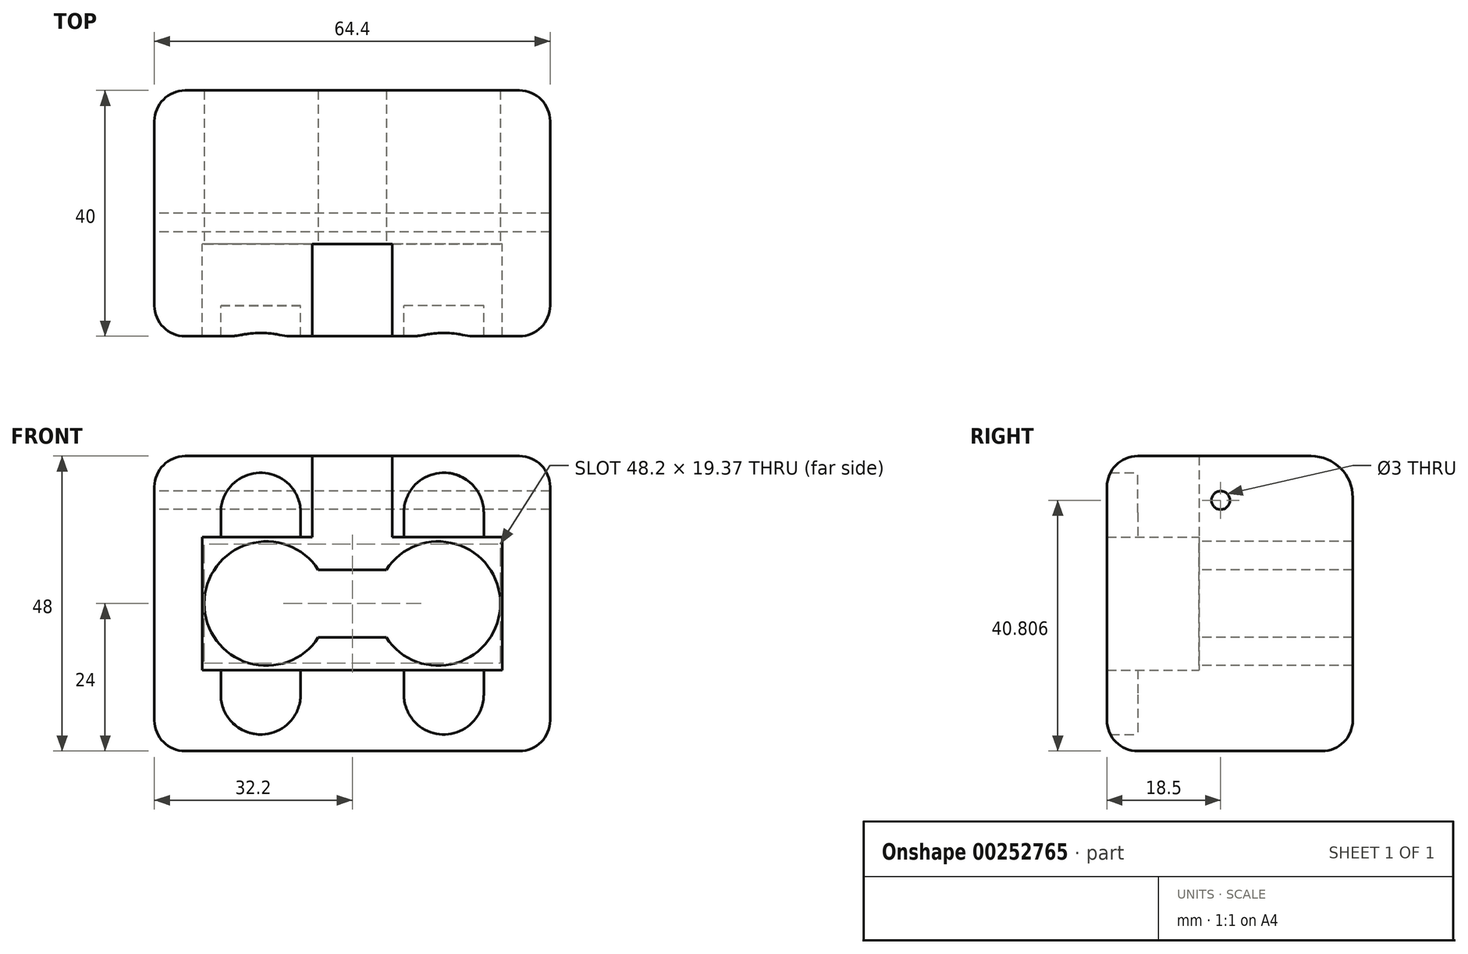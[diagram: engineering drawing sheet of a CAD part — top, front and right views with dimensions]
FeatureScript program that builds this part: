
annotation { "Feature Type Name" : "Feature", "Feature Type Description" : "" }
export const myFeature = defineFeature(function(context is Context, id is Id, definition is map)
    precondition{}
    {
        {
            var Q0;
            Q0=qCreatedBy(makeId("Front.planeOp"),FACE);
            var sketch = newSketch(context, id + "F0", { "sketchPlane" : qUnion([Q0])});
            skLineSegment(sketch, "E0.bottom", {"start": v(32.2, 24) * mm, "end": v(-32.2, 24) * mm});
            skLineSegment(sketch, "E0.top", {"start": v(32.2, -24) * mm, "end": v(-32.2, -24) * mm});
            skLineSegment(sketch, "E0.left", {"start": v(32.2, 24) * mm, "end": v(32.2, -24) * mm});
            skLineSegment(sketch, "E0.right", {"start": v(-32.2, 24) * mm, "end": v(-32.2, -24) * mm});
            skPoint(sketch, "E0.middle", {"position": v(0, 0) * mm});
            skLineSegment(sketch, "E1.bottom", {"start": v(24.4, 10.8) * mm, "end": v(21.4, 10.8) * mm});
            skLineSegment(sketch, "E1.top", {"start": v(24.4, -10.8) * mm, "end": v(21.4, -10.8) * mm});
            skLineSegment(sketch, "E1.left", {"start": v(24.4, 10.8) * mm, "end": v(24.4, -10.8) * mm});
            skLineSegment(sketch, "E1.right", {"start": v(-24.4, 10.8) * mm, "end": v(-24.4, -10.8) * mm});
            skLineSegment(sketch, "E2", {"start": v(-6.5, 24) * mm, "end": v(-6.5, 10.8) * mm});
            skPoint(sketch, "E3", {"position": v(0, 24) * mm});
            skLineSegment(sketch, "E4.MirrorCS", {"start": v(6.5, 24) * mm, "end": v(6.5, 10.8) * mm});
            skLineSegment(sketch, "E5", {"start": v(-21.4, 10.8) * mm, "end": v(-21.4, 14.8) * mm});
            skLineSegment(sketch, "E6", {"start": v(-8.4, 14.8) * mm, "end": v(-8.4, 10.8) * mm});
            skArc(sketch, "E7", {"start": v(-8.4, 14.8) * mm, "mid": v(-14.9, 21.3) * mm, "end": v(-21.4, 14.8) * mm});
            skLineSegment(sketch, "E8.trimOffspring", {"start": v(-21.4, 10.8) * mm, "end": v(-24.4, 10.8) * mm});
            skLineSegment(sketch, "E9.MirrorCS", {"start": v(21.4, 10.8) * mm, "end": v(21.4, 14.8) * mm});
            skArc(sketch, "E10.MirrorCS", {"start": v(8.4, 14.8) * mm, "mid": v(14.9, 21.3) * mm, "end": v(21.4, 14.8) * mm});
            skLineSegment(sketch, "E11.MirrorCS", {"start": v(8.4, 14.8) * mm, "end": v(8.4, 10.8) * mm});
            skLineSegment(sketch, "E12.MirrorCS", {"start": v(-21.4, -10.8) * mm, "end": v(-21.4, -14.8) * mm});
            skArc(sketch, "E13.MirrorCS", {"start": v(-8.4, -14.8) * mm, "mid": v(-14.9, -21.3) * mm, "end": v(-21.4, -14.8) * mm});
            skLineSegment(sketch, "E14.MirrorCS", {"start": v(-8.4, -14.8) * mm, "end": v(-8.4, -10.8) * mm});
            skLineSegment(sketch, "E15.MirrorCS", {"start": v(8.4, -14.8) * mm, "end": v(8.4, -10.8) * mm});
            skArc(sketch, "E16.MirrorCS", {"start": v(8.4, -14.8) * mm, "mid": v(14.9, -21.3) * mm, "end": v(21.4, -14.8) * mm});
            skLineSegment(sketch, "E17.MirrorCS", {"start": v(21.4, -10.8) * mm, "end": v(21.4, -14.8) * mm});
            skLineSegment(sketch, "E18.trimOffspring", {"start": v(8.4, 10.8) * mm, "end": v(6.5, 10.8) * mm});
            skLineSegment(sketch, "E19.trimOffspring", {"start": v(8.4, -10.8) * mm, "end": v(-8.4, -10.8) * mm});
            skLineSegment(sketch, "E20.trimOffspring", {"start": v(-21.4, -10.8) * mm, "end": v(-24.4, -10.8) * mm});
            skLineSegment(sketch, "E21.trimOffspring", {"start": v(-6.5, 10.8) * mm, "end": v(-8.4, 10.8) * mm});
            skSolve(sketch);
        }
        {
            var Q0;
            Q0=makeQuery(id+"F0.imprint","IMPRINT",FACE,{"disambiguationData":[TD([[makeQuery(id+"F0.imprint","IMPRINT",EDGE,{"derivedFrom":sQuery(id+"F0.wireOp",EDGE,"E0.top")}),-1.0]])]});
            extrude(context, id + "F1", {"entities" : qUnion([Q0]), "depth" : 5 * mm});
        }
        {
            var Q0;
            Q0=makeQuery(id+"F1.opExtrude","CAP_FACE",FACE,{"disambiguationData":[OSD([sQuery(id+"F0.wireOp",EDGE,"E0.bottom"),sQuery(id+"F0.wireOp",EDGE,"E0.top"),sQuery(id+"F0.wireOp",EDGE,"E0.left"),sQuery(id+"F0.wireOp",EDGE,"E0.right"),sQuery(id+"F0.wireOp",EDGE,"E1.bottom"),sQuery(id+"F0.wireOp",EDGE,"E1.top"),sQuery(id+"F0.wireOp",EDGE,"E1.left"),sQuery(id+"F0.wireOp",EDGE,"E1.right"),sQuery(id+"F0.wireOp",EDGE,"E2"),sQuery(id+"F0.wireOp",EDGE,"E4.MirrorCS"),sQuery(id+"F0.wireOp",EDGE,"E5"),sQuery(id+"F0.wireOp",EDGE,"E6"),sQuery(id+"F0.wireOp",EDGE,"E7"),sQuery(id+"F0.wireOp",EDGE,"E8.trimOffspring"),sQuery(id+"F0.wireOp",EDGE,"E9.MirrorCS"),sQuery(id+"F0.wireOp",EDGE,"E10.MirrorCS"),sQuery(id+"F0.wireOp",EDGE,"E11.MirrorCS"),sQuery(id+"F0.wireOp",EDGE,"E12.MirrorCS"),sQuery(id+"F0.wireOp",EDGE,"E13.MirrorCS"),sQuery(id+"F0.wireOp",EDGE,"E14.MirrorCS"),sQuery(id+"F0.wireOp",EDGE,"E15.MirrorCS"),sQuery(id+"F0.wireOp",EDGE,"E16.MirrorCS"),sQuery(id+"F0.wireOp",EDGE,"E17.MirrorCS"),sQuery(id+"F0.wireOp",EDGE,"E18.trimOffspring"),sQuery(id+"F0.wireOp",EDGE,"E19.trimOffspring"),sQuery(id+"F0.wireOp",EDGE,"E20.trimOffspring"),sQuery(id+"F0.wireOp",EDGE,"E21.trimOffspring")])],"isStart":true});
            var sketch = newSketch(context, id + "F2", { "sketchPlane" : qUnion([Q0])});
            skLineSegment(sketch, "E22.bottom", {"start": v(24.4, -10.8) * mm, "end": v(-24.4, -10.8) * mm});
            skLineSegment(sketch, "E22.top", {"start": v(24.4, 10.8) * mm, "end": v(-24.4, 10.8) * mm});
            skLineSegment(sketch, "E22.left", {"start": v(24.4, -10.8) * mm, "end": v(24.4, 10.8) * mm});
            skLineSegment(sketch, "E22.right", {"start": v(-24.4, -10.8) * mm, "end": v(-24.4, 10.8) * mm});
            skPoint(sketch, "E22.middle", {"position": v(0, 0) * mm});
            skLineSegment(sketch, "E23.bottom", {"start": v(-32.2, 24) * mm, "end": v(32.2, 24) * mm});
            skLineSegment(sketch, "E23.top", {"start": v(-32.2, -24) * mm, "end": v(32.2, -24) * mm});
            skLineSegment(sketch, "E23.left", {"start": v(-32.2, 24) * mm, "end": v(-32.2, -24) * mm});
            skLineSegment(sketch, "E23.right", {"start": v(32.2, 24) * mm, "end": v(32.2, -24) * mm});
            skLineSegment(sketch, "E24", {"start": v(6.5, 10.8) * mm, "end": v(6.5, 24) * mm});
            skLineSegment(sketch, "E25", {"start": v(-6.5, 10.8) * mm, "end": v(-6.5, 24) * mm});
            skSolve(sketch);
        }
        {
            var Q0;
            {var subQ12=sQuery(id+"F2.wireOp",EDGE,"E22.left");Q0=makeQuery(id+"F2.imprint","IMPRINT",FACE,{"disambiguationData":[TD([[makeQuery(id+"F2.imprint","IMPRINT",EDGE,{"derivedFrom":subQ12}),1.0]])]});}
            var Q1;
            {var subQ1=makeQuery(id+"F1.opExtrude","CAP_EDGE",EDGE,{"disambiguationData":[OSD([sQuery(id+"F0.wireOp",EDGE,"E12.MirrorCS")])],"isStart":true});Q1=makeQuery(id+"F2.imprint","IMPRINT",FACE,{"disambiguationData":[TD([[makeQuery(id+"F2.imprint","IMPRINT",EDGE,{"derivedFrom":subQ1}),-1.0]])]});}
            var Q2;
            {var subQ2=makeQuery(id+"F1.opExtrude","CAP_EDGE",EDGE,{"disambiguationData":[OSD([sQuery(id+"F0.wireOp",EDGE,"E15.MirrorCS")])],"isStart":true});Q2=makeQuery(id+"F2.imprint","IMPRINT",FACE,{"disambiguationData":[TD([[makeQuery(id+"F2.imprint","IMPRINT",EDGE,{"derivedFrom":subQ2}),1.0]])]});}
            var Q3;
            {var subQ1=makeQuery(id+"F1.opExtrude","CAP_EDGE",EDGE,{"disambiguationData":[OSD([sQuery(id+"F0.wireOp",EDGE,"E5")])],"isStart":true});Q3=makeQuery(id+"F2.imprint","IMPRINT",FACE,{"disambiguationData":[TD([[makeQuery(id+"F2.imprint","IMPRINT",EDGE,{"derivedFrom":subQ1}),1.0]])]});}
            var Q4;
            {var subQ1=makeQuery(id+"F1.opExtrude","CAP_EDGE",EDGE,{"disambiguationData":[OSD([sQuery(id+"F0.wireOp",EDGE,"E9.MirrorCS")])],"isStart":true});Q4=makeQuery(id+"F2.imprint","IMPRINT",FACE,{"disambiguationData":[TD([[makeQuery(id+"F2.imprint","IMPRINT",EDGE,{"derivedFrom":subQ1}),-1.0]])]});}
            extrude(context, id + "F3", {"entities" : qUnion([Q0, Q1, Q2, Q3, Q4]), "operationType" : NewBodyOperationType.ADD, "depth" : 10 * mm});
        }
        {
            var Q0;
            Q0=makeQuery(id+"F3.opExtrude","CAP_FACE",FACE,{"disambiguationData":[OSD([sQuery(id+"F2.wireOp",EDGE,"E22.bottom"),sQuery(id+"F2.wireOp",EDGE,"E22.top"),sQuery(id+"F2.wireOp",EDGE,"E22.left"),sQuery(id+"F2.wireOp",EDGE,"E22.right"),sQuery(id+"F2.wireOp",EDGE,"E23.bottom"),sQuery(id+"F2.wireOp",EDGE,"E23.top"),sQuery(id+"F2.wireOp",EDGE,"E23.left"),sQuery(id+"F2.wireOp",EDGE,"E23.right"),sQuery(id+"F2.wireOp",EDGE,"E24"),sQuery(id+"F2.wireOp",EDGE,"E25")])],"isStart":false});
            var sketch = newSketch(context, id + "F4", { "sketchPlane" : qUnion([Q0])});
            skCircle(sketch, "E26", {"center": v(14, 0) * mm, "radius": 10.1 * mm});
            skLineSegment(sketch, "E27", {"start": v(5.53, -5.5) * mm, "end": v(0, -5.5) * mm});
            skLineSegment(sketch, "E28.MirrorCS", {"start": v(5.53, 5.5) * mm, "end": v(0, 5.5) * mm});
            skCircle(sketch, "E29.MirrorC", {"center": v(-14, 0) * mm, "radius": 10.1 * mm});
            skLineSegment(sketch, "E30.MirrorCS", {"start": v(-5.53, -5.5) * mm, "end": v(0, -5.5) * mm});
            skLineSegment(sketch, "E31.MirrorCS", {"start": v(-5.53, 5.5) * mm, "end": v(0, 5.5) * mm});
            skLineSegment(sketch, "E32.bottom", {"start": v(32.2, 24) * mm, "end": v(-32.2, 24) * mm});
            skLineSegment(sketch, "E32.top", {"start": v(32.2, -24) * mm, "end": v(-32.2, -24) * mm});
            skLineSegment(sketch, "E32.left", {"start": v(32.2, 24) * mm, "end": v(32.2, -24) * mm});
            skLineSegment(sketch, "E32.right", {"start": v(-32.2, 24) * mm, "end": v(-32.2, -24) * mm});
            skPoint(sketch, "E32.middle", {"position": v(0, 0) * mm});
            skSolve(sketch);
        }
        {
            var Q0;
            Q0=makeQuery(id+"F4.imprint","IMPRINT",FACE,{"disambiguationData":[TD([[makeQuery(id+"F4.imprint","IMPRINT",EDGE,{"derivedFrom":sQuery(id+"F4.wireOp",EDGE,"E32.top")}),1.0]])]});
            var Q1;
            {var subQ10=sQuery(id+"F4.wireOp",EDGE,"E27");Q1=makeQuery(id+"F4.imprint","IMPRINT",FACE,{"disambiguationData":[TD([[makeQuery(id+"F4.imprint","IMPRINT",EDGE,{"derivedFrom":subQ10}),1.0]])]});}
            extrude(context, id + "F5", {"entities" : qUnion([Q0, Q1]), "operationType" : NewBodyOperationType.ADD, "depth" : 25 * mm});
        }
        {
            var Q0;
            Q0=makeQuery(id+"F5.boolean.opBoolean","MERGE",FACE,{"derivedFrom":[makeQuery(id+"F3.boolean.opBoolean","MERGE",FACE,{"derivedFrom":[makeQuery(id+"F1.opExtrude","SWEPT_FACE",FACE,{"disambiguationData":[OSD([sQuery(id+"F0.wireOp",EDGE,"E0.right")])]}),makeQuery(id+"F3.opExtrude","SWEPT_FACE",FACE,{"disambiguationData":[OSD([sQuery(id+"F2.wireOp",EDGE,"E23.right")])]})]}),makeQuery(id+"F5.opExtrude","SWEPT_FACE",FACE,{"disambiguationData":[OSD([sQuery(id+"F4.wireOp",EDGE,"E32.left")])]})]});
            var sketch = newSketch(context, id + "F6", { "sketchPlane" : qUnion([Q0])});
            skCircle(sketch, "E33", {"center": v(-13.5, 16.8) * mm, "radius": 1.5 * mm});
            skCircle(sketch, "E34.MirrorC", {"center": v(-13.5, 31.2) * mm, "radius": 1.5 * mm});
            skSolve(sketch);
        }
        {
            var Q0;
            Q0=makeQuery(id+"F6.imprint","IMPRINT",FACE,{"disambiguationData":[TD([[makeQuery(id+"F6.imprint","IMPRINT",EDGE,{"derivedFrom":sQuery(id+"F6.wireOp",EDGE,"E33")}),1.0]])]});
            extrude(context, id + "F7", {"entities" : qUnion([Q0]), "operationType" : NewBodyOperationType.REMOVE, "oppositeDirection" : true, "depth" : 69.4 * mm});
        }
        {
            var Q0;
            Q0=makeQuery(id+"F5.opExtrude","CAP_EDGE",EDGE,{"disambiguationData":[OSD([sQuery(id+"F4.wireOp",EDGE,"E32.bottom")])],"isStart":false});
            fillet(context, id + "F8", {"entities" : qUnion([Q0]), "radius" : 6.76 * mm, "tangentPropagation" : true, "allowEdgeOverflow" : false});
        }
        {
            var Q0;
            Q0=makeQuery(id+"F8.opFillet","BLEND_EDGE",EDGE,{"blendedFrom":[makeQuery(id+"F5.opExtrude","CAP_EDGE",EDGE,{"disambiguationData":[OSD([sQuery(id+"F4.wireOp",EDGE,"E32.bottom")])],"isStart":false}),makeQuery(id+"F5.boolean.opBoolean","MERGE",FACE,{"derivedFrom":[makeQuery(id+"F3.boolean.opBoolean","MERGE",FACE,{"derivedFrom":[makeQuery(id+"F1.opExtrude","SWEPT_FACE",FACE,{"disambiguationData":[OSD([sQuery(id+"F0.wireOp",EDGE,"E0.left")])]}),makeQuery(id+"F3.opExtrude","SWEPT_FACE",FACE,{"disambiguationData":[OSD([sQuery(id+"F2.wireOp",EDGE,"E23.left")])]})]}),makeQuery(id+"F5.opExtrude","SWEPT_FACE",FACE,{"disambiguationData":[OSD([sQuery(id+"F4.wireOp",EDGE,"E32.right")])]})]})],"blendedInto":[makeQuery(id+"F5.boolean.opBoolean","MERGE",FACE,{"derivedFrom":[makeQuery(id+"F3.boolean.opBoolean","MERGE",FACE,{"derivedFrom":[makeQuery(id+"F1.opExtrude","SWEPT_FACE",FACE,{"disambiguationData":[OSD([sQuery(id+"F0.wireOp",EDGE,"E0.left")])]}),makeQuery(id+"F3.opExtrude","SWEPT_FACE",FACE,{"disambiguationData":[OSD([sQuery(id+"F2.wireOp",EDGE,"E23.left")])]})]}),makeQuery(id+"F5.opExtrude","SWEPT_FACE",FACE,{"disambiguationData":[OSD([sQuery(id+"F4.wireOp",EDGE,"E32.right")])]})]})]});
            var Q1;
            Q1=makeQuery(id+"F5.opExtrude","CAP_EDGE",EDGE,{"disambiguationData":[OSD([sQuery(id+"F4.wireOp",EDGE,"E32.right")])],"isStart":false});
            fillet(context, id + "F9", {"entities" : qUnion([Q0, Q1]), "radius" : 5 * mm, "tangentPropagation" : true, "allowEdgeOverflow" : false});
        }
        {
            var Q0;
            Q0=makeQuery(id+"F5.opExtrude","CAP_EDGE",EDGE,{"disambiguationData":[OSD([sQuery(id+"F4.wireOp",EDGE,"E32.left")])],"isStart":false});
            fillet(context, id + "F10", {"entities" : qUnion([Q0]), "radius" : 5 * mm, "tangentPropagation" : true, "allowEdgeOverflow" : false});
        }
        {
            var Q0;
            {var subQ0=sQuery(id+"F0.wireOp",EDGE,"E0.bottom");Q0=makeQuery(id+"F1.opExtrude","CAP_EDGE",EDGE,{"disambiguationData":[OSD([subQ0]),TDD([makeQuery(id+"F0.imprint","IMPRINT",EDGE,{"disambiguationData":[TD([[makeQuery(id+"F0.imprint","INTERSECT",VERTEX,{"derivedFrom":[subQ0,sQuery(id+"F0.wireOp",EDGE,"E0.right")]}),1.0]])],"derivedFrom":subQ0})])],"isStart":false});}
            var Q1;
            {var subQ0=sQuery(id+"F0.wireOp",EDGE,"E0.bottom");Q1=makeQuery(id+"F1.opExtrude","CAP_EDGE",EDGE,{"disambiguationData":[OSD([subQ0]),TDD([makeQuery(id+"F0.imprint","IMPRINT",EDGE,{"disambiguationData":[TD([[makeQuery(id+"F0.imprint","INTERSECT",VERTEX,{"derivedFrom":[subQ0,sQuery(id+"F0.wireOp",EDGE,"E0.left")]}),-1.0]])],"derivedFrom":subQ0})])],"isStart":false});}
            fillet(context, id + "F11", {"entities" : qUnion([Q0, Q1]), "radius" : 5 * mm, "tangentPropagation" : true, "allowEdgeOverflow" : false});
        }
        {
            var Q0;
            Q0=makeQuery(id+"F5.boolean.opBoolean","MERGE",FACE,{"derivedFrom":[makeQuery(id+"F3.boolean.opBoolean","MERGE",FACE,{"derivedFrom":[makeQuery(id+"F1.opExtrude","SWEPT_FACE",FACE,{"disambiguationData":[OSD([sQuery(id+"F0.wireOp",EDGE,"E0.top")])]}),makeQuery(id+"F3.opExtrude","SWEPT_FACE",FACE,{"disambiguationData":[OSD([sQuery(id+"F2.wireOp",EDGE,"E23.top")])]})]}),makeQuery(id+"F5.opExtrude","SWEPT_FACE",FACE,{"disambiguationData":[OSD([sQuery(id+"F4.wireOp",EDGE,"E32.top")])]})]});
            fillet(context, id + "F12", {"entities" : qUnion([Q0]), "radius" : 5 * mm, "tangentPropagation" : true, "allowEdgeOverflow" : false});
        }
    });
